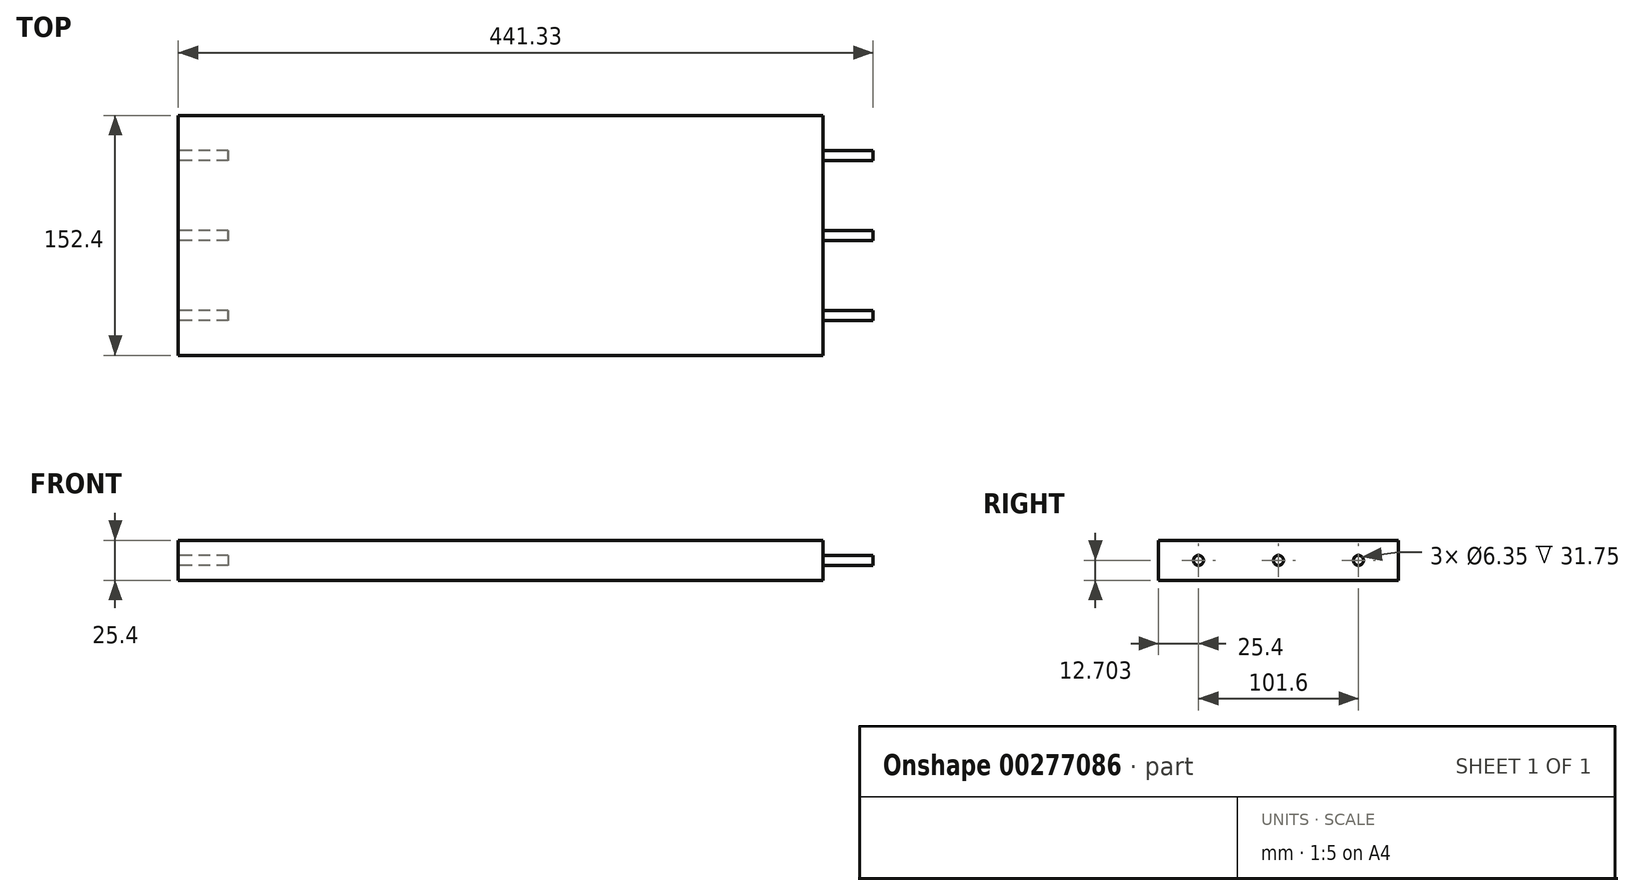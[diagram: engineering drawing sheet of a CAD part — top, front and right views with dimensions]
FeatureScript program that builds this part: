
annotation { "Feature Type Name" : "Feature", "Feature Type Description" : "" }
export const myFeature = defineFeature(function(context is Context, id is Id, definition is map)
    precondition{}
    {
        {
            var Q0;
            Q0=qCreatedBy(makeId("Front.planeOp"),FACE);
            var sketch = newSketch(context, id + "F0", { "sketchPlane" : qUnion([Q0])});
            skLineSegment(sketch, "E0.bottom", {"start": v(-216.98, -19.63) * mm, "end": v(224.35, -19.63) * mm});
            skLineSegment(sketch, "E0.top", {"start": v(-216.98, 5.77) * mm, "end": v(224.35, 5.77) * mm});
            skLineSegment(sketch, "E0.left", {"start": v(-216.98, -19.63) * mm, "end": v(-216.98, 5.77) * mm});
            skLineSegment(sketch, "E0.right", {"start": v(224.35, -19.63) * mm, "end": v(224.35, 5.77) * mm});
            skSolve(sketch);
        }
        {
            var Q0;
            Q0=makeQuery(id+"F0.imprint","IMPRINT",FACE,{"disambiguationData":[TD([[makeQuery(id+"F0.imprint","IMPRINT",EDGE,{"derivedFrom":sQuery(id+"F0.wireOp",EDGE,"E0.bottom")}),1.0]])]});
            extrude(context, id + "F1", {"entities" : qUnion([Q0]), "depth" : 152.4 * mm});
        }
        {
            var Q0;
            Q0=makeQuery(id+"F1.opExtrude","SWEPT_FACE",FACE,{"disambiguationData":[OSD([sQuery(id+"F0.wireOp",EDGE,"E0.left")])]});
            var sketch = newSketch(context, id + "F2", { "sketchPlane" : qUnion([Q0])});
            skCircle(sketch, "E1", {"center": v(25.4, -6.93) * mm, "radius": 3.18 * mm});
            skPoint(sketch, "E1.centerSnap0", {"position": v(0, -6.93) * mm});
            skCircle(sketch, "E2", {"center": v(76.2, -6.93) * mm, "radius": 3.18 * mm});
            skCircle(sketch, "E3", {"center": v(127, -6.93) * mm, "radius": 3.18 * mm});
            skSolve(sketch);
        }
        {
            var Q0;
            Q0=makeQuery(id+"F1.opExtrude","SWEPT_FACE",FACE,{"disambiguationData":[OSD([sQuery(id+"F0.wireOp",EDGE,"E0.right")])]});
            var sketch = newSketch(context, id + "F3", { "sketchPlane" : qUnion([Q0])});
            skCircle(sketch, "E4.0", {"center": v(-127, -6.93) * mm, "radius": 3.18 * mm});
            skCircle(sketch, "E5.0", {"center": v(-76.2, -6.93) * mm, "radius": 3.18 * mm});
            skCircle(sketch, "E6.0", {"center": v(-25.4, -6.93) * mm, "radius": 3.18 * mm});
            skSolve(sketch);
        }
        {
            var Q0;
            Q0=makeQuery(id+"F2.imprint","IMPRINT",FACE,{"disambiguationData":[TD([[makeQuery(id+"F2.imprint","IMPRINT",EDGE,{"derivedFrom":sQuery(id+"F2.wireOp",EDGE,"E1")}),1.0]])]});
            var Q1;
            Q1=makeQuery(id+"F2.imprint","IMPRINT",FACE,{"disambiguationData":[TD([[makeQuery(id+"F2.imprint","IMPRINT",EDGE,{"derivedFrom":sQuery(id+"F2.wireOp",EDGE,"E2")}),1.0]])]});
            var Q2;
            Q2=makeQuery(id+"F2.imprint","IMPRINT",FACE,{"disambiguationData":[TD([[makeQuery(id+"F2.imprint","IMPRINT",EDGE,{"derivedFrom":sQuery(id+"F2.wireOp",EDGE,"E3")}),1.0]])]});
            extrude(context, id + "F4", {"entities" : qUnion([Q0, Q1, Q2]), "operationType" : NewBodyOperationType.REMOVE, "oppositeDirection" : true, "depth" : 31.75 * mm});
        }
        {
            var Q0;
            Q0=makeQuery(id+"F3.imprint","IMPRINT",FACE,{"disambiguationData":[TD([[makeQuery(id+"F3.imprint","IMPRINT",EDGE,{"derivedFrom":sQuery(id+"F3.wireOp",EDGE,"E6.0")}),-1.0]])]});
            var Q1;
            Q1=makeQuery(id+"F3.imprint","IMPRINT",FACE,{"disambiguationData":[TD([[makeQuery(id+"F3.imprint","IMPRINT",EDGE,{"derivedFrom":sQuery(id+"F3.wireOp",EDGE,"E5.0")}),-1.0]])]});
            var Q2;
            Q2=makeQuery(id+"F3.imprint","IMPRINT",FACE,{"disambiguationData":[TD([[makeQuery(id+"F3.imprint","IMPRINT",EDGE,{"derivedFrom":sQuery(id+"F3.wireOp",EDGE,"E4.0")}),-1.0]])]});
            extrude(context, id + "F5", {"entities" : qUnion([Q0, Q1, Q2]), "operationType" : NewBodyOperationType.REMOVE, "oppositeDirection" : true, "depth" : 31.75 * mm});
        }
    });
